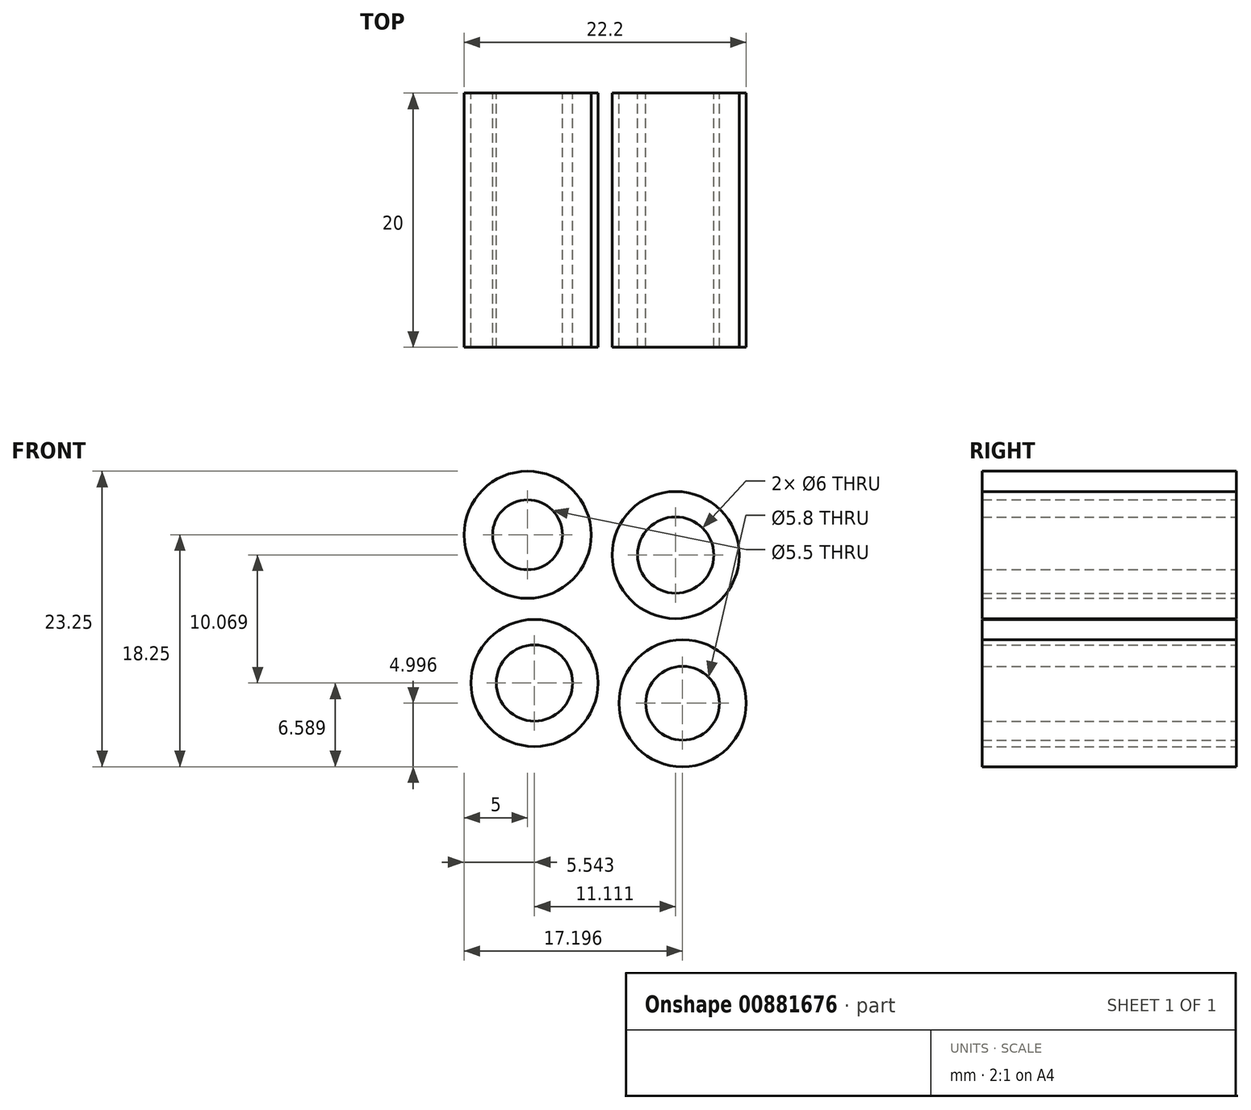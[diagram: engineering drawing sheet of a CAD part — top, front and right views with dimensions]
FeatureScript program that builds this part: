
annotation { "Feature Type Name" : "Feature", "Feature Type Description" : "" }
export const myFeature = defineFeature(function(context is Context, id is Id, definition is map)
    precondition{}
    {
        {
            var Q0;
            Q0=qCreatedBy(makeId("Front.planeOp"),FACE);
            var sketch = newSketch(context, id + "F0", { "sketchPlane" : qUnion([Q0])});
            skCircle(sketch, "E0", {"center": v(0, 0) * mm, "radius": 5 * mm});
            skCircle(sketch, "E1", {"center": v(0, 0) * mm, "radius": 2.75 * mm});
            skCircle(sketch, "E2", {"center": v(11.65, -1.6) * mm, "radius": 5 * mm});
            skCircle(sketch, "E3", {"center": v(11.65, -1.6) * mm, "radius": 3 * mm});
            skCircle(sketch, "E4", {"center": v(0.54, -11.66) * mm, "radius": 5 * mm});
            skCircle(sketch, "E5", {"center": v(0.54, -11.66) * mm, "radius": 3 * mm});
            skCircle(sketch, "E6", {"center": v(12.2, -13.25) * mm, "radius": 5 * mm});
            skCircle(sketch, "E7", {"center": v(12.2, -13.25) * mm, "radius": 2.9 * mm});
            skSolve(sketch);
        }
        {
            var Q0;
            Q0 = qSketchRegion(id + "F0", true);
            extrude(context, id + "F1", {"entities" : qUnion([Q0]), "depth" : 20 * mm, "offsetDistance" : 25 * mm});
        }
    });
